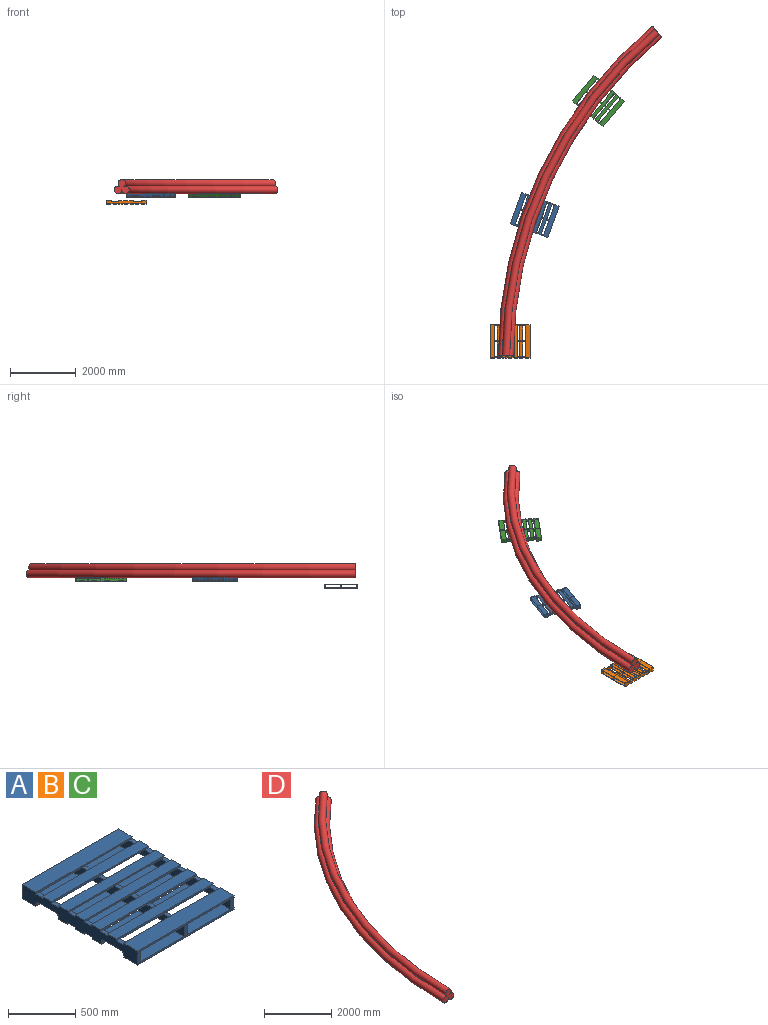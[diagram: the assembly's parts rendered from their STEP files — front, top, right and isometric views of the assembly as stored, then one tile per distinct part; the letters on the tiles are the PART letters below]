
ASSEMBLY  parts=4 mates=3
PART A: 134 faces, bbox 1016x1219.2x127 mm
  f0: plane 71.8x35mm, normal (0,0,1), area 2513mm2, adj f32,f52,f123,f130
  f1: plane 71.8x35mm, normal (0,0,1), area 2513mm2, adj f68,f69,f123,f130
  f2: plane 71.8x35mm, normal (0,0,1), area 2513mm2, adj f29,f85,f123,f130
  f3: plane 74.8x35mm, normal (0,0,1), area 2618mm2, adj f32,f52,f118,f125
  f4: plane 74.8x35mm, normal (0,0,1), area 2618mm2, adj f68,f69,f118,f125
  f5: plane 74.8x35mm, normal (0,0,1), area 2618mm2, adj f29,f85,f118,f125
  f6: plane 74.8x35mm, normal (0,0,1), area 2618mm2, adj f32,f52,f113,f120
  f7: plane 74.8x35mm, normal (0,0,1), area 2618mm2, adj f68,f69,f113,f120
  f8: plane 74.8x35mm, normal (0,0,1), area 2618mm2, adj f29,f85,f113,f120
  f9: plane 74.8x35mm, normal (0,0,1), area 2618mm2, adj f32,f52,f108,f115
  f10: plane 74.8x35mm, normal (0,0,1), area 2618mm2, adj f68,f69,f108,f115
  f11: plane 74.8x35mm, normal (0,0,1), area 2618mm2, adj f29,f85,f108,f115
  f12: plane 74.8x35mm, normal (0,0,1), area 2618mm2, adj f32,f52,f103,f110
  f13: plane 74.8x35mm, normal (0,0,1), area 2618mm2, adj f32,f52,f105,f126
  f14: plane 74.8x35mm, normal (0,0,1), area 2618mm2, adj f68,f69,f103,f110
  f15: plane 74.8x35mm, normal (0,0,1), area 2618mm2, adj f68,f69,f105,f126
  f16: plane 74.8x35mm, normal (0,0,1), area 2618mm2, adj f29,f85,f103,f110
  f17: plane 74.8x35mm, normal (0,0,1), area 2618mm2, adj f29,f85,f105,f126
  f18: plane 35x0.5mm, normal (0,0,-1), area 17.5mm2, adj f32,f37,f52,f98
  f19: plane 35x0.5mm, normal (0,0,-1), area 17.5mm2, adj f53,f68,f69,f98
  f20: plane 35x0.5mm, normal (0,0,-1), area 17.5mm2, adj f29,f70,f85,f98
  f21: plane 85.2x35mm, normal (0,0,-1), area 2982mm2, adj f32,f52,f93,f100
  f22: plane 85.2x35mm, normal (0,0,-1), area 2982mm2, adj f68,f69,f93,f100
  f23: plane 85.2x35mm, normal (0,0,-1), area 2982mm2, adj f29,f85,f93,f100
  f24: plane 85.2x35mm, normal (0,0,-1), area 2982mm2, adj f32,f52,f88,f95
  f25: plane 85.2x35mm, normal (0,0,-1), area 2982mm2, adj f68,f69,f88,f95
  f26: plane 85.2x35mm, normal (0,0,-1), area 2982mm2, adj f29,f85,f88,f95
  f27: plane 1016x16mm, normal (0,1,0), area 16256mm2, adj f28,f29,f30,f32,f45,f61,f78
  f28: plane 1016x146.2mm, normal (0,0,1), area 133198.7mm2, adj f27,f29,f31,f32,f44,f52,f60,f68
  f29: plane 1219.2x127mm, normal (-1,0,0), area 123447.7mm2, adj f2,f5,f8,f11,f16,f17,f20,f23
  f30: plane 1016x146.2mm, normal (0,0,-1), area 148539.2mm2, adj f27,f29,f31,f32
  f31: plane 1016x16mm, normal (0,-1,0), area 16256mm2, adj f28,f29,f30,f32
  f32: plane 1219.2x127mm, normal (1,0,0), area 123447.7mm2, adj f0,f3,f6,f9,f12,f13,f18,f21
  f33: plane 1016x16mm, normal (0,1,0), area 16256mm2, adj f29,f32,f34,f35
  f34: plane 1016x146.2mm, normal (0,0,1), area 133198.7mm2, adj f29,f32,f33,f36,f43,f52,f59,f68
  f35: plane 1016x146.2mm, normal (0,0,-1), area 148539.2mm2, adj f29,f32,f33,f36
  f36: plane 1016x16mm, normal (0,-1,0), area 16256mm2, adj f29,f32,f34,f35,f42,f58,f75
  f37: plane 35x12.2mm, normal (0,1,0), area 427mm2, adj f18,f32,f38,f52
  f38: cylinder r=19mm len=35mm, axis (-1,0,0), area 1044.6mm2, adj f32,f37,f39,f52
  f39: plane 191x35mm, normal (0,0,-1), area 6685mm2, adj f32,f38,f40,f52
  f40: cylinder r=19mm len=35mm, axis (-1,0,0), area 1044.6mm2, adj f32,f39,f41,f52
  f41: plane 35x12.2mm, normal (0,-1,0), area 427mm2, adj f32,f40,f42,f52
  f42: plane 35x5.9mm, normal (0,0,-1), area 206.5mm2, adj f32,f36,f41,f52
  f43: plane 95x35mm, normal (0,1,0), area 3325mm2, adj f32,f34,f52,f132
  f44: plane 95x35mm, normal (0,-1,0), area 3325mm2, adj f28,f32,f52,f128
  f45: plane 35x5.9mm, normal (0,0,-1), area 206.5mm2, adj f27,f32,f46,f52
  f46: plane 35x12.2mm, normal (0,1,0), area 427mm2, adj f32,f45,f47,f52
  f47: cylinder r=19mm len=35mm, axis (-1,0,0), area 1044.6mm2, adj f32,f46,f48,f52
  f48: plane 191x35mm, normal (0,0,-1), area 6685mm2, adj f32,f47,f49,f52
  f49: cylinder r=19mm len=35mm, axis (-1,0,0), area 1044.6mm2, adj f32,f48,f50,f52
  f50: plane 35x12.2mm, normal (0,-1,0), area 427mm2, adj f32,f49,f51,f52
  f51: plane 35x0.5mm, normal (0,0,-1), area 17.5mm2, adj f32,f50,f52,f90
  f52: plane 1219x95mm, normal (-1,0,0), area 101825.3mm2, adj f0,f3,f6,f9,f12,f13,f18,f21
  f53: plane 35x12.2mm, normal (0,1,0), area 427mm2, adj f19,f54,f68,f69
  f54: cylinder r=19mm len=35mm, axis (-1,0,0), area 1044.6mm2, adj f53,f55,f68,f69
  f55: plane 191x35mm, normal (0,0,-1), area 6685mm2, adj f54,f56,f68,f69
  f56: cylinder r=19mm len=35mm, axis (-1,0,0), area 1044.6mm2, adj f55,f57,f68,f69
  f57: plane 35x12.2mm, normal (0,-1,0), area 427mm2, adj f56,f58,f68,f69
  f58: plane 35x5.9mm, normal (0,0,-1), area 206.5mm2, adj f36,f57,f68,f69
  f59: plane 95x35mm, normal (0,1,0), area 3325mm2, adj f34,f68,f69,f132
  f60: plane 95x35mm, normal (0,-1,0), area 3325mm2, adj f28,f68,f69,f128
  f61: plane 35x5.9mm, normal (0,0,-1), area 206.5mm2, adj f27,f62,f68,f69
  f62: plane 35x12.2mm, normal (0,1,0), area 427mm2, adj f61,f63,f68,f69
  f63: cylinder r=19mm len=35mm, axis (-1,0,0), area 1044.6mm2, adj f62,f64,f68,f69
  f64: plane 191x35mm, normal (0,0,-1), area 6685mm2, adj f63,f65,f68,f69
  f65: cylinder r=19mm len=35mm, axis (-1,0,0), area 1044.6mm2, adj f64,f66,f68,f69
  f66: plane 35x12.2mm, normal (0,-1,0), area 427mm2, adj f65,f67,f68,f69
  f67: plane 35x0.5mm, normal (0,0,-1), area 17.5mm2, adj f66,f68,f69,f90
  f68: plane 1219x95mm, normal (1,0,0), area 101825.3mm2, adj f1,f4,f7,f10,f14,f15,f19,f22
  f69: plane 1219x95mm, normal (-1,0,0), area 101825.3mm2, adj f1,f4,f7,f10,f14,f15,f19,f22
  f70: plane 35x12.2mm, normal (0,1,0), area 427mm2, adj f20,f29,f71,f85
  f71: cylinder r=19mm len=35mm, axis (-1,0,0), area 1044.6mm2, adj f29,f70,f72,f85
  f72: plane 191x35mm, normal (0,0,-1), area 6685mm2, adj f29,f71,f73,f85
  f73: cylinder r=19mm len=35mm, axis (-1,0,0), area 1044.6mm2, adj f29,f72,f74,f85
  f74: plane 35x12.2mm, normal (0,-1,0), area 427mm2, adj f29,f73,f75,f85
  f75: plane 35x5.9mm, normal (0,0,-1), area 206.5mm2, adj f29,f36,f74,f85
  f76: plane 95x35mm, normal (0,1,0), area 3325mm2, adj f29,f34,f85,f132
  f77: plane 95x35mm, normal (0,-1,0), area 3325mm2, adj f28,f29,f85,f128
  f78: plane 35x5.9mm, normal (0,0,-1), area 206.5mm2, adj f27,f29,f79,f85
  f79: plane 35x12.2mm, normal (0,1,0), area 427mm2, adj f29,f78,f80,f85
  f80: cylinder r=19mm len=35mm, axis (-1,0,0), area 1044.6mm2, adj f29,f79,f81,f85
  f81: plane 191x35mm, normal (0,0,-1), area 6685mm2, adj f29,f80,f82,f85
  f82: cylinder r=19mm len=35mm, axis (-1,0,0), area 1044.6mm2, adj f29,f81,f83,f85
  f83: plane 35x12.2mm, normal (0,-1,0), area 427mm2, adj f29,f82,f84,f85
  f84: plane 35x0.5mm, normal (0,0,-1), area 17.5mm2, adj f29,f83,f85,f90
  f85: plane 1219x95mm, normal (1,0,0), area 101825.3mm2, adj f2,f5,f8,f11,f16,f17,f20,f23
  f86: plane 455.5x95.2mm, normal (0,0,1), area 43363.6mm2, adj f52,f68,f88,f90
  f87: plane 455.5x95.2mm, normal (0,0,1), area 43363.6mm2, adj f69,f85,f88,f90
  f88: plane 1016x16mm, normal (0,1,0), area 16256mm2, adj f24,f25,f26,f29,f32,f86,f87,f89
  f89: plane 1016x95.2mm, normal (0,0,-1), area 96723.2mm2, adj f29,f32,f88,f90
  f90: plane 1016x16mm, normal (0,-1,0), area 16256mm2, adj f29,f32,f51,f67,f84,f86,f87,f89
  f91: plane 455.5x95.2mm, normal (0,0,1), area 43363.6mm2, adj f52,f68,f93,f95
  f92: plane 455.5x95.2mm, normal (0,0,1), area 43363.6mm2, adj f69,f85,f93,f95
  f93: plane 1016x16mm, normal (0,1,0), area 16256mm2, adj f21,f22,f23,f29,f32,f91,f92,f94
  f94: plane 1016x95.2mm, normal (0,0,-1), area 96723.2mm2, adj f29,f32,f93,f95
  f95: plane 1016x16mm, normal (0,-1,0), area 16256mm2, adj f24,f25,f26,f29,f32,f91,f92,f94
  f96: plane 455.5x95.2mm, normal (0,0,1), area 43363.6mm2, adj f52,f68,f98,f100
  f97: plane 455.5x95.2mm, normal (0,0,1), area 43363.6mm2, adj f69,f85,f98,f100
  f98: plane 1016x16mm, normal (0,1,0), area 16256mm2, adj f18,f19,f20,f29,f32,f96,f97,f99
  f99: plane 1016x95.2mm, normal (0,0,-1), area 96723.2mm2, adj f29,f32,f98,f100
  f100: plane 1016x16mm, normal (0,-1,0), area 16256mm2, adj f21,f22,f23,f29,f32,f96,f97,f99
  f101: plane 455.5x96.2mm, normal (0,0,-1), area 43819.1mm2, adj f52,f68,f103,f105
  f102: plane 455.5x96.2mm, normal (0,0,-1), area 43819.1mm2, adj f69,f85,f103,f105
  f103: plane 1016x16mm, normal (0,1,0), area 16256mm2, adj f12,f14,f16,f29,f32,f101,f102,f104
  f104: plane 1016x96.2mm, normal (0,0,1), area 97739.2mm2, adj f29,f32,f103,f105
  f105: plane 1016x16mm, normal (0,-1,0), area 16256mm2, adj f13,f15,f17,f29,f32,f101,f102,f104
  f106: plane 455.5x96.2mm, normal (0,0,-1), area 43819.1mm2, adj f52,f68,f108,f110
  f107: plane 455.5x96.2mm, normal (0,0,-1), area 43819.1mm2, adj f69,f85,f108,f110
  f108: plane 1016x16mm, normal (0,1,0), area 16256mm2, adj f9,f10,f11,f29,f32,f106,f107,f109
  f109: plane 1016x96.2mm, normal (0,0,1), area 97739.2mm2, adj f29,f32,f108,f110
  f110: plane 1016x16mm, normal (0,-1,0), area 16256mm2, adj f12,f14,f16,f29,f32,f106,f107,f109
  f111: plane 455.5x96.2mm, normal (0,0,-1), area 43819.1mm2, adj f52,f68,f113,f115
  f112: plane 455.5x96.2mm, normal (0,0,-1), area 43819.1mm2, adj f69,f85,f113,f115
  f113: plane 1016x16mm, normal (0,1,0), area 16256mm2, adj f6,f7,f8,f29,f32,f111,f112,f114
  f114: plane 1016x96.2mm, normal (0,0,1), area 97739.2mm2, adj f29,f32,f113,f115
  f115: plane 1016x16mm, normal (0,-1,0), area 16256mm2, adj f9,f10,f11,f29,f32,f111,f112,f114
  f116: plane 455.5x96.2mm, normal (0,0,-1), area 43819.1mm2, adj f52,f68,f118,f120
  f117: plane 455.5x96.2mm, normal (0,0,-1), area 43819.1mm2, adj f69,f85,f118,f120
  f118: plane 1016x16mm, normal (0,1,0), area 16256mm2, adj f3,f4,f5,f29,f32,f116,f117,f119
  f119: plane 1016x96.2mm, normal (0,0,1), area 97739.2mm2, adj f29,f32,f118,f120
  f120: plane 1016x16mm, normal (0,-1,0), area 16256mm2, adj f6,f7,f8,f29,f32,f116,f117,f119
  f121: plane 455.5x96.2mm, normal (0,0,-1), area 43819.1mm2, adj f52,f68,f123,f125
  f122: plane 455.5x96.2mm, normal (0,0,-1), area 43819.1mm2, adj f69,f85,f123,f125
  f123: plane 1016x16mm, normal (0,1,0), area 16256mm2, adj f0,f1,f2,f29,f32,f121,f122,f124
  f124: plane 1016x96.2mm, normal (0,0,1), area 97739.2mm2, adj f29,f32,f123,f125
  f125: plane 1016x16mm, normal (0,-1,0), area 16256mm2, adj f3,f4,f5,f29,f32,f121,f122,f124
  f126: plane 1016x16mm, normal (0,1,0), area 16256mm2, adj f13,f15,f17,f29,f32,f127,f128
  f127: plane 1016x146.2mm, normal (0,0,1), area 148539.2mm2, adj f29,f32,f126,f129
  f128: plane 1016x146.2mm, normal (0,0,-1), area 133198.7mm2, adj f29,f32,f44,f52,f60,f68,f69,f77
  f129: plane 1016x16mm, normal (0,-1,0), area 16256mm2, adj f29,f32,f127,f128
  f130: plane 1016x16mm, normal (0,-1,0), area 16256mm2, adj f0,f1,f2,f29,f32,f131,f132
  f131: plane 1016x146.2mm, normal (0,0,1), area 148539.2mm2, adj f29,f32,f130,f133
  f132: plane 1016x146.2mm, normal (0,0,-1), area 133198.7mm2, adj f29,f32,f43,f52,f59,f68,f69,f76
  f133: plane 1016x16mm, normal (0,1,0), area 16256mm2, adj f29,f32,f131,f132
PART B: same geometry as A
PART C: same geometry as A
PART D: 5 faces, bbox 6070.9x10883.7x429.2 mm
  f0: plane 460x429.19mm, normal (0,-1,0), area 126775.3mm2, adj f2,f3,f4
  f1: plane 429.19x352.68mm, normal (0.77,0.64,0), area 126775.3mm2, adj f2,f3,f4
  f2: torus R=13000mm, axis (0,0,-1), area 6848975.9mm2, adj f0,f1,f3,f4
  f3: torus R=12885mm, axis (0,0,-1), area 6778470.9mm2, adj f0,f1,f2,f4
  f4: torus R=12770mm, axis (0,0,-1), area 6707966mm2, adj f0,f1,f2,f3
PLACE A rot(axis=(0,0,1),70deg) t=(2168.9,4435.79,-231.57)mm
PLACE B rot(axis=(0.71,0.71,0),180deg) t=(1416.16,580.99,-321.07)mm
PLACE C rot(axis=(0,0,1),50deg) t=(4112.34,7910.88,-249.07)mm
PLACE D t=(1172.76,145.66,-7.07)mm
MATE parallel A.f131 <-> D.f2  axis (0,0,1) through (1664.75,4619.28,-104.57)mm
MATE parallel B.f29 <-> D.f0  axis (0,-1,0) through (952.76,72.99,-337.07)mm
MATE parallel C.f131 <-> D.f2  axis (0,0,1) through (3701.36,8255.74,-122.07)mm
